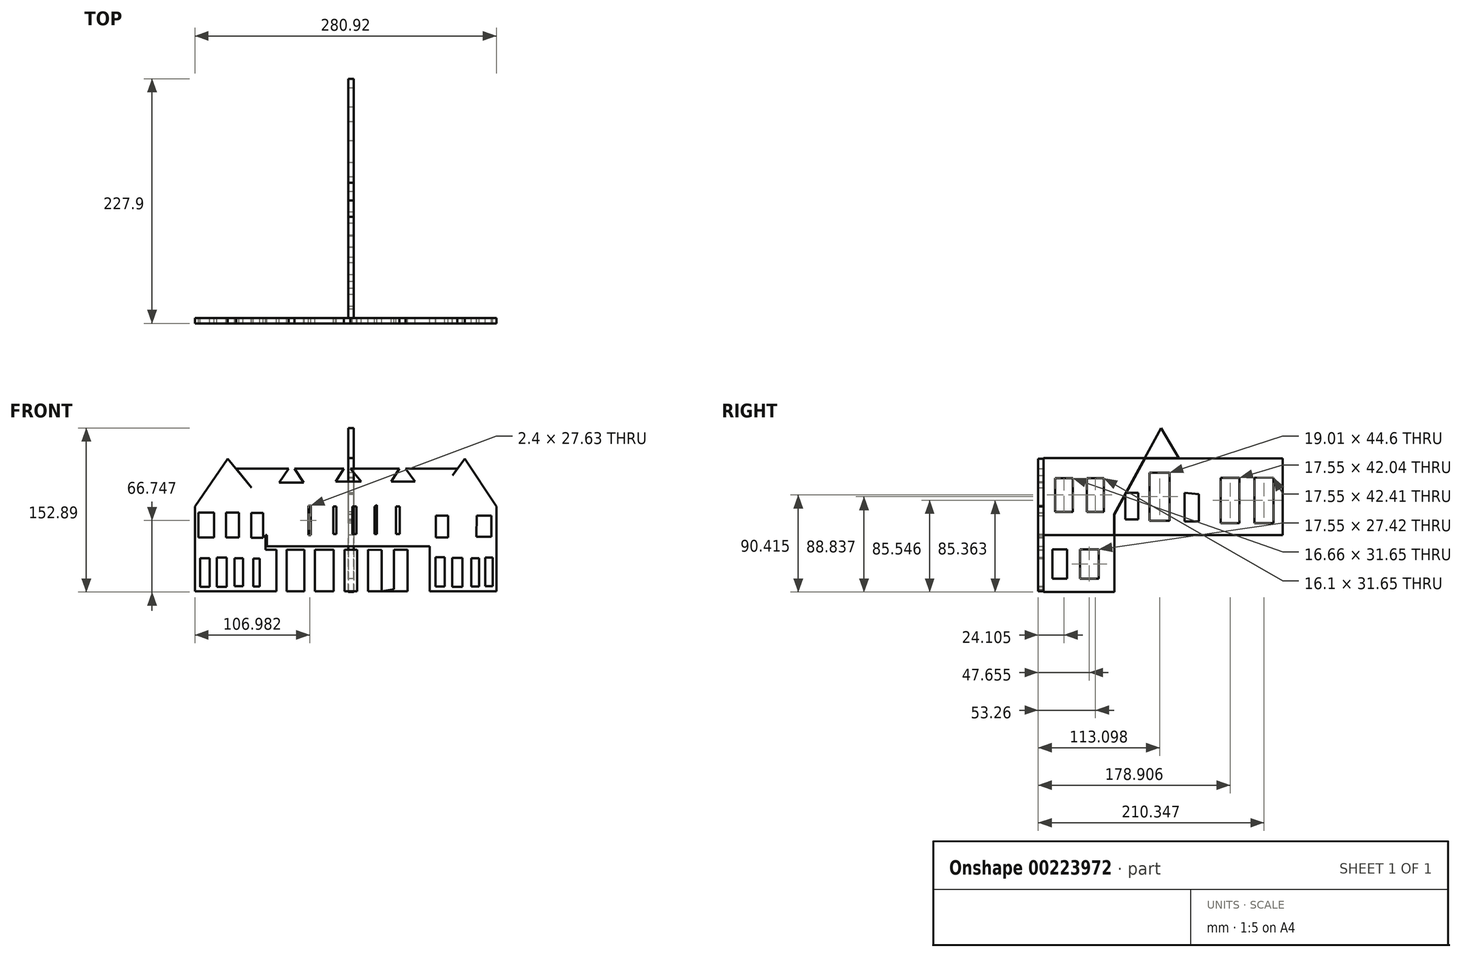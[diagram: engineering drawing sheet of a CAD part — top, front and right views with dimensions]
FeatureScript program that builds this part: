
annotation { "Feature Type Name" : "Feature", "Feature Type Description" : "" }
export const myFeature = defineFeature(function(context is Context, id is Id, definition is map)
    precondition{}
    {
        {
            var Q0;
            Q0=qCreatedBy(makeId("Front.planeOp"),FACE);
            var sketch = newSketch(context, id + "F0", { "sketchPlane" : qUnion([Q0])});
            skLineSegment(sketch, "E0", {"start": v(-37.14, 37.72) * mm, "end": v(-37.14, 10.33) * mm});
            skLineSegment(sketch, "E1", {"start": v(-37.14, 10.33) * mm, "end": v(-34.74, 10.33) * mm});
            skLineSegment(sketch, "E2", {"start": v(-34.74, 10.33) * mm, "end": v(-34.74, 37.96) * mm});
            skLineSegment(sketch, "E3", {"start": v(-34.74, 37.96) * mm, "end": v(-37.14, 37.72) * mm});
            skLineSegment(sketch, "E4", {"start": v(-13.83, 37.24) * mm, "end": v(-13.83, 11.3) * mm});
            skLineSegment(sketch, "E5", {"start": v(-13.83, 11.3) * mm, "end": v(-11.19, 11.3) * mm});
            skLineSegment(sketch, "E6", {"start": v(-11.19, 11.3) * mm, "end": v(-11.19, 37.24) * mm});
            skLineSegment(sketch, "E7", {"start": v(-11.19, 37.24) * mm, "end": v(-13.83, 37.24) * mm});
            skLineSegment(sketch, "E8", {"start": v(3.95, 37.24) * mm, "end": v(3.95, 11.3) * mm});
            skLineSegment(sketch, "E9", {"start": v(3.95, 11.3) * mm, "end": v(7.55, 11.3) * mm});
            skLineSegment(sketch, "E10", {"start": v(7.55, 37.24) * mm, "end": v(3.95, 37.24) * mm});
            skLineSegment(sketch, "E11", {"start": v(7.55, 11.3) * mm, "end": v(7.55, 37.24) * mm});
            skLineSegment(sketch, "E12", {"start": v(24.61, 37.24) * mm, "end": v(24.61, 11.3) * mm});
            skLineSegment(sketch, "E13", {"start": v(24.61, 11.3) * mm, "end": v(26.77, 11.3) * mm});
            skLineSegment(sketch, "E14", {"start": v(26.77, 11.3) * mm, "end": v(26.77, 38.44) * mm});
            skLineSegment(sketch, "E15", {"start": v(26.77, 38.44) * mm, "end": v(24.61, 37.24) * mm});
            skLineSegment(sketch, "E16", {"start": v(44.55, 37.24) * mm, "end": v(44.55, 11.3) * mm});
            skLineSegment(sketch, "E17", {"start": v(44.55, 11.3) * mm, "end": v(47.92, 11.3) * mm});
            skLineSegment(sketch, "E18", {"start": v(47.92, 11.3) * mm, "end": v(47.92, 37.24) * mm});
            skLineSegment(sketch, "E19", {"start": v(47.92, 37.24) * mm, "end": v(44.55, 37.24) * mm});
            skLineSegment(sketch, "E20", {"start": v(77.21, 37.32) * mm, "end": v(107.92, 81.53) * mm});
            skLineSegment(sketch, "E21", {"start": v(107.92, 81.53) * mm, "end": v(138.2, 37.32) * mm});
            skLineSegment(sketch, "E22", {"start": v(138.2, 37.32) * mm, "end": v(77.21, 37.32) * mm});
            skLineSegment(sketch, "E23", {"start": v(138.2, 37.32) * mm, "end": v(138.2, -40.87) * mm});
            skLineSegment(sketch, "E24", {"start": v(138.2, -40.87) * mm, "end": v(77.21, -40.87) * mm});
            skLineSegment(sketch, "E25", {"start": v(-75.9, 37.32) * mm, "end": v(-111.92, 81.53) * mm});
            skLineSegment(sketch, "E26", {"start": v(-111.92, 81.53) * mm, "end": v(-142.62, 37.32) * mm});
            skLineSegment(sketch, "E27", {"start": v(-142.62, 37.32) * mm, "end": v(-75.9, 37.32) * mm});
            skLineSegment(sketch, "E28", {"start": v(-142.62, 29.95) * mm, "end": v(-142.62, 37.32) * mm});
            skLineSegment(sketch, "E29", {"start": v(-142.62, 29.95) * mm, "end": v(-142.62, -40.87) * mm});
            skLineSegment(sketch, "E30", {"start": v(-142.62, -40.87) * mm, "end": v(-75.9, -40.87) * mm});
            skLineSegment(sketch, "E31", {"start": v(-75.9, -40.87) * mm, "end": v(-75.9, 37.32) * mm});
            skLineSegment(sketch, "E32", {"start": v(77.21, -40.87) * mm, "end": v(77.21, 37.32) * mm});
            skLineSegment(sketch, "E33", {"start": v(-104.51, 72.44) * mm, "end": v(101.6, 72.44) * mm});
            skLineSegment(sketch, "E34", {"start": v(-64.56, 59.42) * mm, "end": v(-52.67, 76.55) * mm});
            skPoint(sketch, "E34.startSnap0", {"position": v(-93.9, 59.42) * mm});
            skLineSegment(sketch, "E35", {"start": v(-52.67, 76.55) * mm, "end": v(-41.62, 59.42) * mm});
            skLineSegment(sketch, "E36", {"start": v(-41.62, 59.42) * mm, "end": v(-64.56, 59.42) * mm});
            skLineSegment(sketch, "E37", {"start": v(-11.64, 60.24) * mm, "end": v(-1.45, 76.55) * mm});
            skPoint(sketch, "E37.endSnap0", {"position": v(-1.45, 72.44) * mm});
            skLineSegment(sketch, "E38", {"start": v(-1.45, 76.55) * mm, "end": v(12.22, 60.24) * mm});
            skLineSegment(sketch, "E39", {"start": v(12.22, 60.24) * mm, "end": v(-11.64, 60.24) * mm});
            skLineSegment(sketch, "E40", {"start": v(40.06, 60.24) * mm, "end": v(50.24, 76.55) * mm});
            skLineSegment(sketch, "E41", {"start": v(50.24, 76.55) * mm, "end": v(62.39, 60.24) * mm});
            skLineSegment(sketch, "E42", {"start": v(62.39, 60.24) * mm, "end": v(40.06, 60.24) * mm});
            skLineSegment(sketch, "E43", {"start": v(-142.62, 0) * mm, "end": v(138.2, 0) * mm});
            skLineSegment(sketch, "E44", {"start": v(81.05, 28.12) * mm, "end": v(81.05, 7.63) * mm});
            skLineSegment(sketch, "E45", {"start": v(93.28, 7.63) * mm, "end": v(93.28, 28.12) * mm});
            skLineSegment(sketch, "E46", {"start": v(93.28, 28.12) * mm, "end": v(81.05, 28.12) * mm});
            skLineSegment(sketch, "E47", {"start": v(81.05, 7.63) * mm, "end": v(93.28, 7.63) * mm});
            skLineSegment(sketch, "E48", {"start": v(101.54, 7.63) * mm, "end": v(101.54, 28.43) * mm});
            skLineSegment(sketch, "E49", {"start": v(101.54, 28.43) * mm, "end": v(114.08, 28.43) * mm});
            skLineSegment(sketch, "E50", {"start": v(114.08, 28.43) * mm, "end": v(114.08, 7.63) * mm});
            skLineSegment(sketch, "E51", {"start": v(114.08, 7.63) * mm, "end": v(101.54, 7.63) * mm});
            skLineSegment(sketch, "E52", {"start": v(123.26, 28.43) * mm, "end": v(133.66, 28.43) * mm});
            skLineSegment(sketch, "E53", {"start": v(133.66, 28.43) * mm, "end": v(133.66, 7.63) * mm});
            skLineSegment(sketch, "E54", {"start": v(133.66, 7.63) * mm, "end": v(120.2, 7.63) * mm});
            skLineSegment(sketch, "E55", {"start": v(120.2, 7.63) * mm, "end": v(120.2, 28.43) * mm});
            skLineSegment(sketch, "E56", {"start": v(120.2, 28.43) * mm, "end": v(123.26, 28.43) * mm});
            skLineSegment(sketch, "E57", {"start": v(120.2, 28.43) * mm, "end": v(120.2, 7.63) * mm});
            skLineSegment(sketch, "E58", {"start": v(-138.59, 30.88) * mm, "end": v(-138.59, 8.24) * mm});
            skLineSegment(sketch, "E59", {"start": v(-138.59, 8.24) * mm, "end": v(-125.74, 8.24) * mm});
            skLineSegment(sketch, "E60", {"start": v(-125.74, 8.24) * mm, "end": v(-125.74, 30.88) * mm});
            skLineSegment(sketch, "E61", {"start": v(-125.74, 30.88) * mm, "end": v(-138.59, 30.88) * mm});
            skLineSegment(sketch, "E62", {"start": v(-114.11, 8.24) * mm, "end": v(-114.11, 30.88) * mm});
            skLineSegment(sketch, "E63", {"start": v(-114.11, 30.88) * mm, "end": v(-102.18, 30.88) * mm});
            skLineSegment(sketch, "E64", {"start": v(-102.18, 30.88) * mm, "end": v(-102.18, 8.24) * mm});
            skLineSegment(sketch, "E65", {"start": v(-102.18, 8.24) * mm, "end": v(-114.11, 8.24) * mm});
            skLineSegment(sketch, "E66", {"start": v(-90.25, 8.24) * mm, "end": v(-90.25, 30.88) * mm});
            skLineSegment(sketch, "E67", {"start": v(-90.25, 30.88) * mm, "end": v(-79.85, 30.88) * mm});
            skLineSegment(sketch, "E68", {"start": v(-79.85, 30.88) * mm, "end": v(-79.85, 8.24) * mm});
            skLineSegment(sketch, "E69", {"start": v(-79.85, 8.24) * mm, "end": v(-90.25, 8.24) * mm});
            skLineSegment(sketch, "E70", {"start": v(-138.28, -20.2) * mm, "end": v(-138.28, -37.03) * mm});
            skLineSegment(sketch, "E71", {"start": v(-138.28, -37.03) * mm, "end": v(-129.71, -37.03) * mm});
            skLineSegment(sketch, "E72", {"start": v(-129.71, -37.03) * mm, "end": v(-129.71, -18.07) * mm});
            skLineSegment(sketch, "E73", {"start": v(-138.28, -20.2) * mm, "end": v(-138.28, -11.34) * mm});
            skLineSegment(sketch, "E74", {"start": v(-138.28, -11.34) * mm, "end": v(-129.71, -11.34) * mm});
            skLineSegment(sketch, "E75", {"start": v(-129.71, -11.34) * mm, "end": v(-129.71, -18.07) * mm});
            skLineSegment(sketch, "E76", {"start": v(-122.07, -37.03) * mm, "end": v(-122.07, -11.03) * mm});
            skLineSegment(sketch, "E77", {"start": v(-122.07, -11.03) * mm, "end": v(-113.5, -11.03) * mm});
            skLineSegment(sketch, "E78", {"start": v(-113.5, -11.03) * mm, "end": v(-113.5, -37.03) * mm});
            skLineSegment(sketch, "E79", {"start": v(-113.5, -37.03) * mm, "end": v(-122.07, -37.03) * mm});
            skLineSegment(sketch, "E80", {"start": v(-105.85, -37.03) * mm, "end": v(-105.85, -11.03) * mm});
            skLineSegment(sketch, "E81", {"start": v(-105.85, -11.03) * mm, "end": v(-97.29, -11.03) * mm});
            skLineSegment(sketch, "E82", {"start": v(-97.29, -11.03) * mm, "end": v(-97.29, -37.03) * mm});
            skLineSegment(sketch, "E83", {"start": v(-97.29, -37.03) * mm, "end": v(-105.85, -37.03) * mm});
            skLineSegment(sketch, "E84", {"start": v(-89.64, -37.03) * mm, "end": v(-89.64, -11.03) * mm});
            skLineSegment(sketch, "E85", {"start": v(-89.64, -11.03) * mm, "end": v(-81.08, -11.03) * mm});
            skLineSegment(sketch, "E86", {"start": v(-81.08, -11.03) * mm, "end": v(-81.08, -37.03) * mm});
            skLineSegment(sketch, "E87", {"start": v(-81.08, -37.03) * mm, "end": v(-89.64, -37.03) * mm});
            skLineSegment(sketch, "E88", {"start": v(81.96, -33.97) * mm, "end": v(81.96, -11.03) * mm});
            skLineSegment(sketch, "E89", {"start": v(81.96, -11.03) * mm, "end": v(89.92, -11.03) * mm});
            skLineSegment(sketch, "E90", {"start": v(89.92, -11.03) * mm, "end": v(89.92, -37.03) * mm});
            skLineSegment(sketch, "E91", {"start": v(81.96, -33.97) * mm, "end": v(81.96, -37.03) * mm});
            skLineSegment(sketch, "E92", {"start": v(81.96, -37.03) * mm, "end": v(89.92, -37.03) * mm});
            skLineSegment(sketch, "E93", {"start": v(96.65, -37.03) * mm, "end": v(96.65, -11.03) * mm});
            skLineSegment(sketch, "E94", {"start": v(96.65, -11.03) * mm, "end": v(106.44, -11.03) * mm});
            skLineSegment(sketch, "E95", {"start": v(106.44, -11.03) * mm, "end": v(106.44, -37.03) * mm});
            skLineSegment(sketch, "E96", {"start": v(96.65, -37.03) * mm, "end": v(106.44, -37.03) * mm});
            skLineSegment(sketch, "E97", {"start": v(114.08, -37.03) * mm, "end": v(114.08, -11.03) * mm});
            skLineSegment(sketch, "E98", {"start": v(114.08, -11.03) * mm, "end": v(121.73, -11.03) * mm});
            skLineSegment(sketch, "E99", {"start": v(121.73, -11.03) * mm, "end": v(121.73, -37.03) * mm});
            skLineSegment(sketch, "E100", {"start": v(121.73, -37.03) * mm, "end": v(114.08, -37.03) * mm});
            skLineSegment(sketch, "E101", {"start": v(127.54, -11.03) * mm, "end": v(127.54, -37.03) * mm});
            skLineSegment(sketch, "E102", {"start": v(127.54, -37.03) * mm, "end": v(134.27, -37.03) * mm});
            skLineSegment(sketch, "E103", {"start": v(134.27, -37.03) * mm, "end": v(134.27, -11.03) * mm});
            skLineSegment(sketch, "E104", {"start": v(134.27, -11.03) * mm, "end": v(127.54, -11.03) * mm});
            skSolve(sketch);
        }
        {
            var Q0;
            Q0=qCreatedBy(makeId("Right.planeOp"),FACE);
            var sketch = newSketch(context, id + "F1", { "sketchPlane" : qUnion([Q0])});
            skLineSegment(sketch, "E105", {"start": v(0, 82.22) * mm, "end": v(55.54, 82.22) * mm});
            skLineSegment(sketch, "E106", {"start": v(0, 82.22) * mm, "end": v(0, -42.77) * mm});
            skLineSegment(sketch, "E107", {"start": v(0, -42.77) * mm, "end": v(141.8, -42.77) * mm});
            skLineSegment(sketch, "E108", {"start": v(141.8, 82.22) * mm, "end": v(55.54, 82.22) * mm});
            skLineSegment(sketch, "E109", {"start": v(141.8, 82.22) * mm, "end": v(222.59, 82.22) * mm});
            skLineSegment(sketch, "E110", {"start": v(222.59, 82.22) * mm, "end": v(222.59, -42.77) * mm});
            skLineSegment(sketch, "E111", {"start": v(222.59, -42.77) * mm, "end": v(141.8, -42.77) * mm});
            skLineSegment(sketch, "E112", {"start": v(65.67, 29.77) * mm, "end": v(109.54, 110.29) * mm});
            skLineSegment(sketch, "E113", {"start": v(109.54, 110.29) * mm, "end": v(156.19, 29.77) * mm});
            skLineSegment(sketch, "E114", {"start": v(65.67, 29.77) * mm, "end": v(65.67, -42.77) * mm});
            skLineSegment(sketch, "E115", {"start": v(65.67, -42.77) * mm, "end": v(156.19, -42.77) * mm});
            skLineSegment(sketch, "E116", {"start": v(156.19, -42.77) * mm, "end": v(156.19, 29.77) * mm});
            skLineSegment(sketch, "E117", {"start": v(0, 10.33) * mm, "end": v(222.59, 10.33) * mm});
            skLineSegment(sketch, "E118.bottom", {"start": v(10.7, 63.64) * mm, "end": v(27.36, 63.64) * mm});
            skLineSegment(sketch, "E118.top", {"start": v(10.7, 31.99) * mm, "end": v(27.36, 31.99) * mm});
            skLineSegment(sketch, "E118.left", {"start": v(10.7, 63.64) * mm, "end": v(10.7, 31.99) * mm});
            skLineSegment(sketch, "E118.right", {"start": v(27.36, 63.64) * mm, "end": v(27.36, 31.99) * mm});
            skPoint(sketch, "E119.firstSnap0", {"position": v(19.03, 63.64) * mm});
            skLineSegment(sketch, "E119.bottom", {"start": v(40.13, 63.64) * mm, "end": v(56.23, 63.64) * mm});
            skLineSegment(sketch, "E119.top", {"start": v(40.13, 31.99) * mm, "end": v(56.23, 31.99) * mm});
            skLineSegment(sketch, "E119.left", {"start": v(40.13, 63.64) * mm, "end": v(40.13, 31.99) * mm});
            skLineSegment(sketch, "E119.right", {"start": v(56.23, 63.64) * mm, "end": v(56.23, 31.99) * mm});
            skLineSegment(sketch, "E120.bottom", {"start": v(76.55, 49.73) * mm, "end": v(89, 49.73) * mm});
            skLineSegment(sketch, "E120.top", {"start": v(76.55, 24.77) * mm, "end": v(89, 24.77) * mm});
            skLineSegment(sketch, "E120.left", {"start": v(76.55, 49.73) * mm, "end": v(76.55, 24.77) * mm});
            skLineSegment(sketch, "E120.right", {"start": v(89, 49.73) * mm, "end": v(89, 24.77) * mm});
            skLineSegment(sketch, "E121.bottom", {"start": v(99, 68.64) * mm, "end": v(117.32, 68.64) * mm});
            skLineSegment(sketch, "E121.top", {"start": v(99, 24.77) * mm, "end": v(117.32, 24.77) * mm});
            skLineSegment(sketch, "E121.left", {"start": v(99, 68.64) * mm, "end": v(99, 24.77) * mm});
            skLineSegment(sketch, "E121.right", {"start": v(117.32, 68.64) * mm, "end": v(117.32, 24.77) * mm});
            skPoint(sketch, "E122.firstSnap0", {"position": v(82.77, 49.73) * mm});
            skPoint(sketch, "E122.oppositeSnap0", {"position": v(108.15, 24.77) * mm});
            skLineSegment(sketch, "E122.bottom", {"start": v(144.62, 49.73) * mm, "end": v(131.2, 49.73) * mm});
            skLineSegment(sketch, "E122.top", {"start": v(144.62, 24.77) * mm, "end": v(131.2, 24.77) * mm});
            skLineSegment(sketch, "E122.left", {"start": v(144.62, 49.73) * mm, "end": v(144.62, 24.77) * mm});
            skLineSegment(sketch, "E122.right", {"start": v(131.2, 49.73) * mm, "end": v(131.2, 24.77) * mm});
            skLineSegment(sketch, "E123.bottom", {"start": v(213.39, 63.64) * mm, "end": v(195.62, 63.64) * mm});
            skLineSegment(sketch, "E123.top", {"start": v(213.39, 22.55) * mm, "end": v(195.62, 22.55) * mm});
            skLineSegment(sketch, "E123.left", {"start": v(213.39, 63.64) * mm, "end": v(213.39, 22.55) * mm});
            skLineSegment(sketch, "E123.right", {"start": v(195.62, 63.64) * mm, "end": v(195.62, 22.55) * mm});
            skPoint(sketch, "E124.oppositeSnap0", {"position": v(182.2, 82.22) * mm});
            skLineSegment(sketch, "E124.bottom", {"start": v(166.74, 63.64) * mm, "end": v(182.2, 63.64) * mm});
            skLineSegment(sketch, "E124.top", {"start": v(166.74, 22.55) * mm, "end": v(182.2, 22.55) * mm});
            skLineSegment(sketch, "E124.left", {"start": v(166.74, 63.64) * mm, "end": v(166.74, 22.55) * mm});
            skLineSegment(sketch, "E124.right", {"start": v(182.2, 63.64) * mm, "end": v(182.2, 22.55) * mm});
            skLineSegment(sketch, "E125.bottom", {"start": v(7.92, 0) * mm, "end": v(21.8, 0) * mm});
            skLineSegment(sketch, "E125.top", {"start": v(7.92, -29.1) * mm, "end": v(21.8, -29.1) * mm});
            skLineSegment(sketch, "E125.left", {"start": v(7.92, 0) * mm, "end": v(7.92, -29.1) * mm});
            skLineSegment(sketch, "E125.right", {"start": v(21.8, 0) * mm, "end": v(21.8, -29.1) * mm});
            skLineSegment(sketch, "E126.bottom", {"start": v(35.68, -3) * mm, "end": v(51.23, -3) * mm});
            skLineSegment(sketch, "E126.top", {"start": v(35.68, -28.54) * mm, "end": v(51.23, -28.54) * mm});
            skLineSegment(sketch, "E126.left", {"start": v(35.68, -3) * mm, "end": v(35.68, -28.54) * mm});
            skLineSegment(sketch, "E126.right", {"start": v(51.23, -3) * mm, "end": v(51.23, -28.54) * mm});
            skLineSegment(sketch, "E127.bottom", {"start": v(77.33, 0) * mm, "end": v(92.33, 0) * mm});
            skLineSegment(sketch, "E127.top", {"start": v(77.33, -29.65) * mm, "end": v(92.33, -29.65) * mm});
            skLineSegment(sketch, "E127.left", {"start": v(77.33, 0) * mm, "end": v(77.33, -29.65) * mm});
            skLineSegment(sketch, "E127.right", {"start": v(92.33, 0) * mm, "end": v(92.33, -29.65) * mm});
            skLineSegment(sketch, "E128.bottom", {"start": v(106.77, 0) * mm, "end": v(123.43, 0) * mm});
            skLineSegment(sketch, "E128.top", {"start": v(106.77, -29.65) * mm, "end": v(123.43, -29.65) * mm});
            skLineSegment(sketch, "E128.left", {"start": v(106.77, 0) * mm, "end": v(106.77, -29.65) * mm});
            skLineSegment(sketch, "E128.right", {"start": v(123.43, 0) * mm, "end": v(123.43, -29.65) * mm});
            skLineSegment(sketch, "E129.bottom", {"start": v(134.53, 0) * mm, "end": v(149.53, 0) * mm});
            skLineSegment(sketch, "E129.top", {"start": v(134.53, -29.65) * mm, "end": v(149.53, -29.65) * mm});
            skLineSegment(sketch, "E129.left", {"start": v(134.53, 0) * mm, "end": v(134.53, -29.65) * mm});
            skLineSegment(sketch, "E129.right", {"start": v(149.53, 0) * mm, "end": v(149.53, -29.65) * mm});
            skLineSegment(sketch, "E130.bottom", {"start": v(166.74, 0) * mm, "end": v(184.51, 0) * mm});
            skLineSegment(sketch, "E130.top", {"start": v(166.74, -29.65) * mm, "end": v(184.51, -29.65) * mm});
            skLineSegment(sketch, "E130.left", {"start": v(166.74, 0) * mm, "end": v(166.74, -29.65) * mm});
            skLineSegment(sketch, "E130.right", {"start": v(184.51, 0) * mm, "end": v(184.51, -29.65) * mm});
            skLineSegment(sketch, "E131.bottom", {"start": v(198.4, 0) * mm, "end": v(215.05, 0) * mm});
            skLineSegment(sketch, "E131.top", {"start": v(198.4, -29.65) * mm, "end": v(215.05, -29.65) * mm});
            skLineSegment(sketch, "E131.left", {"start": v(198.4, 0) * mm, "end": v(198.4, -29.65) * mm});
            skLineSegment(sketch, "E131.right", {"start": v(215.05, 0) * mm, "end": v(215.05, -29.65) * mm});
            skSolve(sketch);
        }
        {
            var Q0;
            Q0=qCreatedBy(makeId("Right.planeOp"),FACE);
            var sketch = newSketch(context, id + "F2", { "sketchPlane" : qUnion([Q0])});
            skLineSegment(sketch, "E132", {"start": v(3.1, 82.07) * mm, "end": v(222.82, 82.07) * mm});
            skLineSegment(sketch, "E133", {"start": v(222.82, 82.07) * mm, "end": v(222.82, -42.6) * mm});
            skLineSegment(sketch, "E134", {"start": v(222.82, -42.6) * mm, "end": v(0, -42.6) * mm});
            skLineSegment(sketch, "E135", {"start": v(0, -42.6) * mm, "end": v(0, 79.14) * mm});
            skLineSegment(sketch, "E136", {"start": v(27.22, 64.15) * mm, "end": v(11.13, 64.15) * mm});
            skLineSegment(sketch, "E137", {"start": v(11.13, 64.15) * mm, "end": v(11.13, 31.61) * mm});
            skLineSegment(sketch, "E138", {"start": v(11.13, 31.61) * mm, "end": v(27.59, 31.61) * mm});
            skLineSegment(sketch, "E139", {"start": v(27.59, 31.61) * mm, "end": v(27.22, 64.15) * mm});
            skLineSegment(sketch, "E140", {"start": v(56.83, 64.15) * mm, "end": v(56.83, 32.34) * mm});
            skLineSegment(sketch, "E141", {"start": v(56.83, 32.34) * mm, "end": v(40.38, 32.34) * mm});
            skLineSegment(sketch, "E142", {"start": v(40.38, 32.34) * mm, "end": v(40.38, 64.15) * mm});
            skLineSegment(sketch, "E143", {"start": v(40.38, 64.15) * mm, "end": v(56.83, 64.15) * mm});
            skLineSegment(sketch, "E144", {"start": v(109.48, 109.85) * mm, "end": v(156.28, 28.32) * mm});
            skLineSegment(sketch, "E145", {"start": v(156.28, 28.32) * mm, "end": v(156.28, -42.6) * mm});
            skLineSegment(sketch, "E146", {"start": v(109.48, 109.85) * mm, "end": v(65.97, 29.42) * mm});
            skLineSegment(sketch, "E147", {"start": v(65.97, 29.42) * mm, "end": v(65.97, -42.6) * mm});
            skLineSegment(sketch, "E148", {"start": v(222.82, 10.4) * mm, "end": v(0, 10.4) * mm});
            skLineSegment(sketch, "E149", {"start": v(3.1, 0) * mm, "end": v(222.82, 0) * mm});
            skLineSegment(sketch, "E150", {"start": v(222.82, 0) * mm, "end": v(215.87, 0) * mm});
            skLineSegment(sketch, "E151", {"start": v(215.87, 0) * mm, "end": v(215.87, -28.35) * mm});
            skLineSegment(sketch, "E152", {"start": v(215.87, -28.35) * mm, "end": v(198.32, -28.35) * mm});
            skLineSegment(sketch, "E153", {"start": v(198.32, -28.35) * mm, "end": v(198.32, 0) * mm});
            skLineSegment(sketch, "E154", {"start": v(198.32, 0) * mm, "end": v(186.26, 0) * mm});
            skLineSegment(sketch, "E155", {"start": v(186.26, 0) * mm, "end": v(186.26, -29.44) * mm});
            skLineSegment(sketch, "E156", {"start": v(186.26, -29.44) * mm, "end": v(166.15, -29.44) * mm});
            skLineSegment(sketch, "E157", {"start": v(166.15, -29.44) * mm, "end": v(166.15, 0) * mm});
            skLineSegment(sketch, "E158", {"start": v(166.15, 0) * mm, "end": v(149.33, 0) * mm});
            skLineSegment(sketch, "E159", {"start": v(149.33, 0) * mm, "end": v(149.33, -29.8) * mm});
            skLineSegment(sketch, "E160", {"start": v(149.33, -29.8) * mm, "end": v(134.34, -29.8) * mm});
            skLineSegment(sketch, "E161", {"start": v(134.34, -29.8) * mm, "end": v(134.34, 0) * mm});
            skLineSegment(sketch, "E162", {"start": v(134.34, 0) * mm, "end": v(149.33, 0) * mm});
            skLineSegment(sketch, "E163", {"start": v(124.1, 0) * mm, "end": v(124.1, -30.17) * mm});
            skLineSegment(sketch, "E164", {"start": v(124.1, -30.17) * mm, "end": v(106.19, -30.17) * mm});
            skLineSegment(sketch, "E165", {"start": v(106.19, -30.17) * mm, "end": v(106.19, 0) * mm});
            skLineSegment(sketch, "E166", {"start": v(106.19, 0) * mm, "end": v(124.1, 0) * mm});
            skLineSegment(sketch, "E167", {"start": v(91.57, 0) * mm, "end": v(91.57, -30.17) * mm});
            skLineSegment(sketch, "E168", {"start": v(91.57, -30.17) * mm, "end": v(77.3, -30.17) * mm});
            skLineSegment(sketch, "E169", {"start": v(77.3, -30.17) * mm, "end": v(77.3, 0) * mm});
            skLineSegment(sketch, "E170", {"start": v(77.3, 0) * mm, "end": v(91.57, 0) * mm});
            skLineSegment(sketch, "E171", {"start": v(51.35, -2.75) * mm, "end": v(51.35, -30.17) * mm});
            skPoint(sketch, "E171.endSnap0", {"position": v(84.44, -30.17) * mm});
            skLineSegment(sketch, "E172", {"start": v(51.35, -30.17) * mm, "end": v(33.8, -30.17) * mm});
            skLineSegment(sketch, "E173", {"start": v(33.8, -30.17) * mm, "end": v(33.8, -2.75) * mm});
            skLineSegment(sketch, "E174", {"start": v(33.8, -2.75) * mm, "end": v(51.35, -2.75) * mm});
            skLineSegment(sketch, "E175", {"start": v(21.74, -2.75) * mm, "end": v(21.74, -30.17) * mm});
            skLineSegment(sketch, "E176", {"start": v(21.74, -30.17) * mm, "end": v(8.2, -30.17) * mm});
            skLineSegment(sketch, "E177", {"start": v(8.2, -30.17) * mm, "end": v(8.2, -2.75) * mm});
            skLineSegment(sketch, "E178", {"start": v(8.2, -2.75) * mm, "end": v(21.74, -2.75) * mm});
            skLineSegment(sketch, "E179", {"start": v(214.04, 63.79) * mm, "end": v(214.04, 21.74) * mm});
            skLineSegment(sketch, "E180", {"start": v(214.04, 21.74) * mm, "end": v(196.5, 21.74) * mm});
            skLineSegment(sketch, "E181", {"start": v(196.5, 21.74) * mm, "end": v(196.5, 64.15) * mm});
            skLineSegment(sketch, "E182", {"start": v(196.5, 64.15) * mm, "end": v(214.04, 63.79) * mm});
            skLineSegment(sketch, "E183", {"start": v(182.6, 63.79) * mm, "end": v(182.6, 21.74) * mm});
            skLineSegment(sketch, "E184", {"start": v(182.6, 21.74) * mm, "end": v(165.05, 21.74) * mm});
            skLineSegment(sketch, "E185", {"start": v(165.05, 21.74) * mm, "end": v(165.05, 63.79) * mm});
            skLineSegment(sketch, "E186", {"start": v(165.05, 63.79) * mm, "end": v(182.6, 63.79) * mm});
            skLineSegment(sketch, "E187", {"start": v(117.52, 69.63) * mm, "end": v(117.52, 23.93) * mm});
            skPoint(sketch, "E187.startSnap0", {"position": v(87.73, 69.63) * mm});
            skLineSegment(sketch, "E188", {"start": v(117.52, 23.93) * mm, "end": v(98.51, 23.93) * mm});
            skLineSegment(sketch, "E189", {"start": v(98.51, 23.93) * mm, "end": v(98.51, 68.54) * mm});
            skLineSegment(sketch, "E190", {"start": v(98.51, 68.54) * mm, "end": v(121.18, 68.54) * mm});
            skLineSegment(sketch, "E191", {"start": v(131.42, 49.9) * mm, "end": v(131.42, 23.2) * mm});
            skLineSegment(sketch, "E192", {"start": v(131.42, 23.2) * mm, "end": v(144.58, 23.2) * mm});
            skLineSegment(sketch, "E193", {"start": v(144.58, 23.2) * mm, "end": v(144.58, 48.7) * mm});
            skLineSegment(sketch, "E194", {"start": v(144.58, 48.7) * mm, "end": v(131.42, 49.9) * mm});
            skLineSegment(sketch, "E195", {"start": v(88.28, 49.9) * mm, "end": v(88.28, 25.03) * mm});
            skLineSegment(sketch, "E196", {"start": v(88.28, 25.03) * mm, "end": v(76.21, 25.03) * mm});
            skLineSegment(sketch, "E197", {"start": v(76.21, 25.03) * mm, "end": v(76.21, 49.9) * mm});
            skLineSegment(sketch, "E198", {"start": v(76.21, 49.9) * mm, "end": v(88.28, 49.9) * mm});
            skSolve(sketch);
        }
        {
            var Q0;
            Q0=qCreatedBy(makeId("Front.planeOp"),FACE);
            var sketch = newSketch(context, id + "F3", { "sketchPlane" : qUnion([Q0])});
            skLineSegment(sketch, "E199", {"start": v(108.7, 81.73) * mm, "end": v(138, 37.2) * mm});
            skLineSegment(sketch, "E200", {"start": v(138, 37.2) * mm, "end": v(138, -41.98) * mm});
            skLineSegment(sketch, "E201", {"start": v(138, -41.98) * mm, "end": v(-142.92, -41.98) * mm});
            skLineSegment(sketch, "E202", {"start": v(-142.92, -41.98) * mm, "end": v(-142.92, 37.2) * mm});
            skLineSegment(sketch, "E203", {"start": v(-142.92, 37.2) * mm, "end": v(-112.46, 81.73) * mm});
            skLineSegment(sketch, "E204", {"start": v(-112.46, 81.73) * mm, "end": v(-75.54, 37.2) * mm});
            skLineSegment(sketch, "E205", {"start": v(-75.54, 37.2) * mm, "end": v(75.96, 37.2) * mm});
            skLineSegment(sketch, "E206", {"start": v(75.96, 37.2) * mm, "end": v(108.7, 81.73) * mm});
            skLineSegment(sketch, "E207", {"start": v(101.98, 72.6) * mm, "end": v(68.73, 72.6) * mm});
            skLineSegment(sketch, "E208", {"start": v(68.73, 72.6) * mm, "end": v(53.5, 72.6) * mm});
            skLineSegment(sketch, "E209", {"start": v(53.5, 72.6) * mm, "end": v(-104.9, 72.6) * mm});
            skLineSegment(sketch, "E210", {"start": v(-51.94, 77.16) * mm, "end": v(-41.66, 58.5) * mm});
            skLineSegment(sketch, "E211", {"start": v(-41.66, 58.5) * mm, "end": v(-65.26, 58.5) * mm});
            skLineSegment(sketch, "E212", {"start": v(-65.26, 58.5) * mm, "end": v(-51.94, 77.16) * mm});
            skLineSegment(sketch, "E213", {"start": v(0, 77.16) * mm, "end": v(13.34, 61.07) * mm});
            skLineSegment(sketch, "E214", {"start": v(13.34, 61.07) * mm, "end": v(-12.35, 61.07) * mm});
            skLineSegment(sketch, "E215", {"start": v(-12.35, 61.07) * mm, "end": v(0, 77.16) * mm});
            skLineSegment(sketch, "E216", {"start": v(50.45, 77.16) * mm, "end": v(63.8, 61.06) * mm});
            skLineSegment(sketch, "E217", {"start": v(63.8, 61.06) * mm, "end": v(40.18, 61.06) * mm});
            skLineSegment(sketch, "E218", {"start": v(40.18, 61.06) * mm, "end": v(49.7, 76.78) * mm});
            skLineSegment(sketch, "E219", {"start": v(138, 37.2) * mm, "end": v(75.96, 37.2) * mm});
            skLineSegment(sketch, "E220", {"start": v(81.67, 28.44) * mm, "end": v(81.67, 8.26) * mm});
            skLineSegment(sketch, "E221", {"start": v(81.67, 8.26) * mm, "end": v(93.09, 8.26) * mm});
            skLineSegment(sketch, "E222", {"start": v(93.09, 8.26) * mm, "end": v(93.09, 28.44) * mm});
            skLineSegment(sketch, "E223", {"start": v(93.09, 28.44) * mm, "end": v(81.67, 28.44) * mm});
            skLineSegment(sketch, "E224", {"start": v(101.84, 28.44) * mm, "end": v(114.78, 28.44) * mm});
            skLineSegment(sketch, "E225", {"start": v(114.78, 28.44) * mm, "end": v(114.78, 7.12) * mm});
            skLineSegment(sketch, "E226", {"start": v(114.78, 7.12) * mm, "end": v(101.08, 7.12) * mm});
            skLineSegment(sketch, "E227", {"start": v(101.08, 7.12) * mm, "end": v(101.46, 27.3) * mm});
            skLineSegment(sketch, "E228", {"start": v(119.73, 28.44) * mm, "end": v(133.44, 28.44) * mm});
            skLineSegment(sketch, "E229", {"start": v(133.44, 28.44) * mm, "end": v(133.44, 9.02) * mm});
            skLineSegment(sketch, "E230", {"start": v(133.44, 9.02) * mm, "end": v(119.35, 9.02) * mm});
            skLineSegment(sketch, "E231", {"start": v(119.35, 9.02) * mm, "end": v(119.73, 28.44) * mm});
            skLineSegment(sketch, "E232", {"start": v(75.96, 37.2) * mm, "end": v(75.96, -41.98) * mm});
            skLineSegment(sketch, "E233", {"start": v(75.96, -41.98) * mm, "end": v(75.96, 10.55) * mm});
            skLineSegment(sketch, "E234", {"start": v(75.96, 10.55) * mm, "end": v(-77.06, 10.55) * mm});
            skLineSegment(sketch, "E235", {"start": v(-77.06, 10.55) * mm, "end": v(-77.06, -3.16) * mm});
            skLineSegment(sketch, "E236", {"start": v(-77.06, -3.16) * mm, "end": v(75.96, -3.16) * mm});
            skLineSegment(sketch, "E237", {"start": v(75.96, -3.16) * mm, "end": v(66.82, -3.16) * mm});
            skLineSegment(sketch, "E238", {"start": v(66.82, -3.16) * mm, "end": v(66.82, -41.98) * mm});
            skLineSegment(sketch, "E239", {"start": v(66.82, -41.98) * mm, "end": v(55.4, -41.98) * mm});
            skLineSegment(sketch, "E240", {"start": v(55.4, -41.98) * mm, "end": v(55.4, -3.16) * mm});
            skLineSegment(sketch, "E241", {"start": v(55.4, -3.16) * mm, "end": v(42.46, -3.16) * mm});
            skLineSegment(sketch, "E242", {"start": v(42.46, -3.16) * mm, "end": v(42.46, -40.08) * mm});
            skLineSegment(sketch, "E243", {"start": v(42.46, -40.08) * mm, "end": v(31.04, -41.98) * mm});
            skLineSegment(sketch, "E244", {"start": v(31.04, -41.98) * mm, "end": v(31.04, -3.54) * mm});
            skLineSegment(sketch, "E245", {"start": v(31.04, -3.54) * mm, "end": v(18.48, -3.16) * mm});
            skLineSegment(sketch, "E246", {"start": v(18.48, -3.16) * mm, "end": v(18.48, -41.98) * mm});
            skLineSegment(sketch, "E247", {"start": v(18.48, -41.98) * mm, "end": v(8.2, -41.98) * mm});
            skLineSegment(sketch, "E248", {"start": v(8.2, -41.98) * mm, "end": v(8.2, -3.16) * mm});
            skLineSegment(sketch, "E249", {"start": v(8.2, -3.16) * mm, "end": v(-3.6, -3.16) * mm});
            skLineSegment(sketch, "E250", {"start": v(-3.6, -3.16) * mm, "end": v(-3.6, -41.98) * mm});
            skLineSegment(sketch, "E251", {"start": v(-13.5, -3.16) * mm, "end": v(-13.5, -41.98) * mm});
            skLineSegment(sketch, "E252", {"start": v(-31, -3.16) * mm, "end": v(-31, -41.98) * mm});
            skLineSegment(sketch, "E253", {"start": v(-40.9, -3.16) * mm, "end": v(-40.9, -41.98) * mm});
            skLineSegment(sketch, "E254", {"start": v(-57.27, -3.16) * mm, "end": v(-57.27, -41.98) * mm});
            skLineSegment(sketch, "E255", {"start": v(-66.79, -3.16) * mm, "end": v(-66.79, -41.98) * mm});
            skLineSegment(sketch, "E256", {"start": v(-77.06, -3.16) * mm, "end": v(-77.06, -41.98) * mm});
            skLineSegment(sketch, "E257", {"start": v(-77.06, -41.98) * mm, "end": v(-75.16, -41.22) * mm});
            skLineSegment(sketch, "E258.bottom", {"start": v(134.58, -10.39) * mm, "end": v(127.73, -10.39) * mm});
            skLineSegment(sketch, "E258.top", {"start": v(134.58, -37.03) * mm, "end": v(127.73, -37.03) * mm});
            skLineSegment(sketch, "E258.left", {"start": v(134.58, -10.39) * mm, "end": v(134.58, -37.03) * mm});
            skLineSegment(sketch, "E258.right", {"start": v(127.73, -10.39) * mm, "end": v(127.73, -37.03) * mm});
            skLineSegment(sketch, "E259.bottom", {"start": v(122.02, -11.15) * mm, "end": v(114.78, -11.15) * mm});
            skLineSegment(sketch, "E259.top", {"start": v(122.02, -37.41) * mm, "end": v(114.78, -37.41) * mm});
            skLineSegment(sketch, "E259.left", {"start": v(122.02, -11.15) * mm, "end": v(122.02, -37.41) * mm});
            skLineSegment(sketch, "E259.right", {"start": v(114.78, -11.15) * mm, "end": v(114.78, -37.41) * mm});
            skLineSegment(sketch, "E260.bottom", {"start": v(106.41, -10.77) * mm, "end": v(96.9, -10.77) * mm});
            skLineSegment(sketch, "E260.top", {"start": v(106.41, -37.8) * mm, "end": v(96.9, -37.8) * mm});
            skLineSegment(sketch, "E260.left", {"start": v(106.41, -10.77) * mm, "end": v(106.41, -37.8) * mm});
            skLineSegment(sketch, "E260.right", {"start": v(96.9, -10.77) * mm, "end": v(96.9, -37.8) * mm});
            skLineSegment(sketch, "E261.bottom", {"start": v(90.04, -10) * mm, "end": v(81.29, -10) * mm});
            skLineSegment(sketch, "E261.top", {"start": v(90.04, -37.41) * mm, "end": v(81.29, -37.41) * mm});
            skLineSegment(sketch, "E261.left", {"start": v(90.04, -10) * mm, "end": v(90.04, -37.41) * mm});
            skLineSegment(sketch, "E261.right", {"start": v(81.29, -10) * mm, "end": v(81.29, -37.41) * mm});
            skLineSegment(sketch, "E262.bottom", {"start": v(-79.35, 31.1) * mm, "end": v(-90.39, 31.1) * mm});
            skLineSegment(sketch, "E262.top", {"start": v(-79.35, 7.88) * mm, "end": v(-90.39, 7.88) * mm});
            skLineSegment(sketch, "E262.left", {"start": v(-79.35, 31.1) * mm, "end": v(-79.35, 7.88) * mm});
            skLineSegment(sketch, "E262.right", {"start": v(-90.39, 31.1) * mm, "end": v(-90.39, 7.88) * mm});
            skLineSegment(sketch, "E263.bottom", {"start": v(-101.8, 31.48) * mm, "end": v(-113.99, 31.48) * mm});
            skLineSegment(sketch, "E263.top", {"start": v(-101.8, 8.26) * mm, "end": v(-113.99, 8.26) * mm});
            skLineSegment(sketch, "E263.left", {"start": v(-101.8, 31.48) * mm, "end": v(-101.8, 8.26) * mm});
            skLineSegment(sketch, "E263.right", {"start": v(-113.99, 31.48) * mm, "end": v(-113.99, 8.26) * mm});
            skLineSegment(sketch, "E264.bottom", {"start": v(-125.03, 31.48) * mm, "end": v(-139.5, 31.48) * mm});
            skLineSegment(sketch, "E264.top", {"start": v(-125.03, 8.26) * mm, "end": v(-139.5, 8.26) * mm});
            skLineSegment(sketch, "E264.left", {"start": v(-125.03, 31.48) * mm, "end": v(-125.03, 8.26) * mm});
            skLineSegment(sketch, "E264.right", {"start": v(-139.5, 31.48) * mm, "end": v(-139.5, 8.26) * mm});
            skLineSegment(sketch, "E265.bottom", {"start": v(-82.4, -11.53) * mm, "end": v(-88.48, -11.53) * mm});
            skLineSegment(sketch, "E265.top", {"start": v(-82.4, -37.41) * mm, "end": v(-88.48, -37.41) * mm});
            skLineSegment(sketch, "E265.left", {"start": v(-82.4, -11.53) * mm, "end": v(-82.4, -37.41) * mm});
            skLineSegment(sketch, "E265.right", {"start": v(-88.48, -11.53) * mm, "end": v(-88.48, -37.41) * mm});
            skLineSegment(sketch, "E266.bottom", {"start": v(-98, -11.15) * mm, "end": v(-106, -11.15) * mm});
            skLineSegment(sketch, "E266.top", {"start": v(-98, -37.03) * mm, "end": v(-106, -37.03) * mm});
            skLineSegment(sketch, "E266.left", {"start": v(-98, -11.15) * mm, "end": v(-98, -37.03) * mm});
            skLineSegment(sketch, "E266.right", {"start": v(-106, -11.15) * mm, "end": v(-106, -37.03) * mm});
            skLineSegment(sketch, "E267.bottom", {"start": v(-113.23, -10.39) * mm, "end": v(-122.36, -10.39) * mm});
            skLineSegment(sketch, "E267.top", {"start": v(-113.23, -37.8) * mm, "end": v(-122.36, -37.8) * mm});
            skLineSegment(sketch, "E267.left", {"start": v(-113.23, -10.39) * mm, "end": v(-113.23, -37.8) * mm});
            skLineSegment(sketch, "E267.right", {"start": v(-122.36, -10.39) * mm, "end": v(-122.36, -37.8) * mm});
            skLineSegment(sketch, "E268.bottom", {"start": v(-129.21, -11.15) * mm, "end": v(-137.97, -11.15) * mm});
            skLineSegment(sketch, "E268.top", {"start": v(-129.21, -37.8) * mm, "end": v(-137.97, -37.8) * mm});
            skLineSegment(sketch, "E268.left", {"start": v(-129.21, -11.15) * mm, "end": v(-129.21, -37.8) * mm});
            skLineSegment(sketch, "E268.right", {"start": v(-137.97, -11.15) * mm, "end": v(-137.97, -37.8) * mm});
            skLineSegment(sketch, "E269.bottom", {"start": v(48.17, 37.2) * mm, "end": v(44.36, 37.2) * mm});
            skLineSegment(sketch, "E269.top", {"start": v(48.17, 10.55) * mm, "end": v(44.36, 10.55) * mm});
            skLineSegment(sketch, "E269.left", {"start": v(48.17, 37.2) * mm, "end": v(48.17, 10.55) * mm});
            skLineSegment(sketch, "E269.right", {"start": v(44.36, 37.2) * mm, "end": v(44.36, 10.55) * mm});
            skLineSegment(sketch, "E270.bottom", {"start": v(27.23, 37.2) * mm, "end": v(24.95, 37.2) * mm});
            skLineSegment(sketch, "E270.top", {"start": v(27.23, 10.55) * mm, "end": v(24.95, 10.55) * mm});
            skLineSegment(sketch, "E270.left", {"start": v(27.23, 37.2) * mm, "end": v(27.23, 10.55) * mm});
            skLineSegment(sketch, "E270.right", {"start": v(24.95, 37.2) * mm, "end": v(24.95, 10.55) * mm});
            skLineSegment(sketch, "E271.bottom", {"start": v(8.2, 37.2) * mm, "end": v(3.63, 37.2) * mm});
            skLineSegment(sketch, "E271.top", {"start": v(8.2, 10.55) * mm, "end": v(3.63, 10.55) * mm});
            skLineSegment(sketch, "E271.left", {"start": v(8.2, 37.2) * mm, "end": v(8.2, 10.55) * mm});
            skLineSegment(sketch, "E271.right", {"start": v(3.63, 37.2) * mm, "end": v(3.63, 10.55) * mm});
            skLineSegment(sketch, "E272.bottom", {"start": v(-11.21, 37.2) * mm, "end": v(-14.26, 37.2) * mm});
            skLineSegment(sketch, "E272.top", {"start": v(-11.21, 10.55) * mm, "end": v(-14.26, 10.55) * mm});
            skLineSegment(sketch, "E272.left", {"start": v(-11.21, 37.2) * mm, "end": v(-11.21, 10.55) * mm});
            skLineSegment(sketch, "E272.right", {"start": v(-14.26, 37.2) * mm, "end": v(-14.26, 10.55) * mm});
            skLineSegment(sketch, "E273.bottom", {"start": v(-35.2, 37.2) * mm, "end": v(-37.1, 37.2) * mm});
            skLineSegment(sketch, "E273.top", {"start": v(-35.2, 10.55) * mm, "end": v(-37.1, 10.55) * mm});
            skLineSegment(sketch, "E273.left", {"start": v(-35.2, 37.2) * mm, "end": v(-35.2, 10.55) * mm});
            skLineSegment(sketch, "E273.right", {"start": v(-37.1, 37.2) * mm, "end": v(-37.1, 10.55) * mm});
            skLineSegment(sketch, "E274.bottom", {"start": v(-53.46, 37.2) * mm, "end": v(-57.27, 37.2) * mm});
            skLineSegment(sketch, "E274.top", {"start": v(-53.46, 10.55) * mm, "end": v(-57.27, 10.55) * mm});
            skLineSegment(sketch, "E274.left", {"start": v(-53.46, 37.2) * mm, "end": v(-53.46, 10.55) * mm});
            skLineSegment(sketch, "E274.right", {"start": v(-57.27, 37.2) * mm, "end": v(-57.27, 10.55) * mm});
            skLineSegment(sketch, "E275", {"start": v(-142.92, 37.2) * mm, "end": v(-75.54, 37.2) * mm});
            skLineSegment(sketch, "E276", {"start": v(-142.92, 0) * mm, "end": v(138, 0) * mm});
            skSolve(sketch);
        }
        {
            var Q0;
            Q0=makeQuery(id+"F0.imprint","IMPRINT",FACE,{"disambiguationData":[TD([[makeQuery(id+"F0.imprint","IMPRINT",EDGE,{"derivedFrom":sQuery(id+"F0.wireOp",EDGE,"E0")}),-1.0]])]});
            extrude(context, id + "F4", {"entities" : qUnion([Q0]), "depth" : 5.08 * mm});
        }
        {
            var Q0;
            {var subQ0=sQuery(id+"F3.wireOp",EDGE,"E203");Q0=makeQuery(id+"F3.imprint","IMPRINT",FACE,{"disambiguationData":[TD([[makeQuery(id+"F3.imprint","IMPRINT",EDGE,{"derivedFrom":subQ0}),-1.0]])]});}
            var Q1;
            Q1=makeQuery(id+"F3.imprint","IMPRINT",FACE,{"disambiguationData":[TD([[makeQuery(id+"F3.imprint","IMPRINT",EDGE,{"derivedFrom":sQuery(id+"F3.wireOp",EDGE,"E262.bottom")}),-1.0]])]});
            var Q2;
            {var subQ5=sQuery(id+"F3.wireOp",EDGE,"E256");Q2=makeQuery(id+"F3.imprint","IMPRINT",FACE,{"disambiguationData":[TD([[makeQuery(id+"F3.imprint","IMPRINT",EDGE,{"derivedFrom":subQ5}),-1.0]])]});}
            var Q3;
            {var subQ0=sQuery(id+"F3.wireOp",EDGE,"E199");Q3=makeQuery(id+"F3.imprint","IMPRINT",FACE,{"disambiguationData":[TD([[makeQuery(id+"F3.imprint","IMPRINT",EDGE,{"derivedFrom":subQ0}),-1.0]])]});}
            var Q4;
            Q4=makeQuery(id+"F3.imprint","IMPRINT",FACE,{"disambiguationData":[TD([[makeQuery(id+"F3.imprint","IMPRINT",EDGE,{"derivedFrom":sQuery(id+"F3.wireOp",EDGE,"E258.bottom")}),-1.0]])]});
            var Q5;
            {var subQ0=sQuery(id+"F3.wireOp",EDGE,"E255");Q5=makeQuery(id+"F3.imprint","IMPRINT",FACE,{"disambiguationData":[TD([[makeQuery(id+"F3.imprint","IMPRINT",EDGE,{"derivedFrom":subQ0}),-1.0]])]});}
            var Q6;
            {var subQ0=sQuery(id+"F3.wireOp",EDGE,"E253");Q6=makeQuery(id+"F3.imprint","IMPRINT",FACE,{"disambiguationData":[TD([[makeQuery(id+"F3.imprint","IMPRINT",EDGE,{"derivedFrom":subQ0}),-1.0]])]});}
            var Q7;
            {var subQ0=sQuery(id+"F3.wireOp",EDGE,"E251");Q7=makeQuery(id+"F3.imprint","IMPRINT",FACE,{"disambiguationData":[TD([[makeQuery(id+"F3.imprint","IMPRINT",EDGE,{"derivedFrom":subQ0}),-1.0]])]});}
            var Q8;
            {var subQ0=sQuery(id+"F3.wireOp",EDGE,"E244");Q8=makeQuery(id+"F3.imprint","IMPRINT",FACE,{"disambiguationData":[TD([[makeQuery(id+"F3.imprint","IMPRINT",EDGE,{"derivedFrom":subQ0}),1.0]])]});}
            var Q9;
            {var subQ0=sQuery(id+"F3.wireOp",EDGE,"E240");Q9=makeQuery(id+"F3.imprint","IMPRINT",FACE,{"disambiguationData":[TD([[makeQuery(id+"F3.imprint","IMPRINT",EDGE,{"derivedFrom":subQ0}),1.0]])]});}
            var Q10;
            {var subQ4=sQuery(id+"F3.wireOp",EDGE,"E237");Q10=makeQuery(id+"F3.imprint","IMPRINT",FACE,{"disambiguationData":[TD([[makeQuery(id+"F3.imprint","IMPRINT",EDGE,{"derivedFrom":subQ4}),1.0]])]});}
            var Q11;
            {var subQ0=sQuery(id+"F3.wireOp",EDGE,"E248");Q11=makeQuery(id+"F3.imprint","IMPRINT",FACE,{"disambiguationData":[TD([[makeQuery(id+"F3.imprint","IMPRINT",EDGE,{"derivedFrom":subQ0}),1.0]])]});}
            var Q12;
            {var subQ1=sQuery(id+"F3.wireOp",EDGE,"E219");Q12=makeQuery(id+"F3.imprint","IMPRINT",FACE,{"disambiguationData":[TD([[makeQuery(id+"F3.imprint","IMPRINT",EDGE,{"derivedFrom":subQ1}),1.0]])]});}
            extrude(context, id + "F5", {"entities" : qUnion([Q0, Q1, Q2, Q3, Q4, Q5, Q6, Q7, Q8, Q9, Q10, Q11, Q12]), "operationType" : NewBodyOperationType.ADD, "depth" : 5.08 * mm});
        }
        {
            var Q0;
            {var subQ10=sQuery(id+"F1.wireOp",EDGE,"E105");Q0=makeQuery(id+"F1.imprint","IMPRINT",FACE,{"disambiguationData":[TD([[makeQuery(id+"F1.imprint","IMPRINT",EDGE,{"derivedFrom":subQ10}),-1.0]])]});}
            var Q1;
            Q1=makeQuery(id+"F2.imprint","IMPRINT",FACE,{"disambiguationData":[TD([[makeQuery(id+"F2.imprint","IMPRINT",EDGE,{"derivedFrom":sQuery(id+"F2.wireOp",EDGE,"E171")}),1.0]])]});
            var Q2;
            {var subQ0=sQuery(id+"F2.wireOp",EDGE,"E188");Q2=makeQuery(id+"F2.imprint","IMPRINT",FACE,{"disambiguationData":[TD([[makeQuery(id+"F2.imprint","IMPRINT",EDGE,{"derivedFrom":subQ0}),1.0]])]});}
            var Q3;
            {var subQ0=sQuery(id+"F1.wireOp",EDGE,"E113");var subQ1=sQuery(id+"F1.wireOp",EDGE,"E108");var subQ2=makeQuery(id+"F1.imprint","INTERSECT",VERTEX,{"derivedFrom":[subQ1,subQ0]});Q3=makeQuery(id+"F1.imprint","IMPRINT",FACE,{"disambiguationData":[TD([[makeQuery(id+"F1.imprint","IMPRINT",EDGE,{"disambiguationData":[TD([[subQ2,-1.0]])],"derivedFrom":subQ1}),-1.0]])]});}
            var Q4;
            Q4=makeQuery(id+"F2.imprint","IMPRINT",FACE,{"disambiguationData":[TD([[makeQuery(id+"F2.imprint","IMPRINT",EDGE,{"derivedFrom":sQuery(id+"F2.wireOp",EDGE,"E179")}),1.0]])]});
            var Q5;
            {var subQ10=sQuery(id+"F2.wireOp",EDGE,"E150");Q5=makeQuery(id+"F2.imprint","IMPRINT",FACE,{"disambiguationData":[TD([[makeQuery(id+"F2.imprint","IMPRINT",EDGE,{"derivedFrom":subQ10}),-1.0]])]});}
            var Q6;
            {var subQ0=sQuery(id+"F1.wireOp",EDGE,"E115");Q6=makeQuery(id+"F1.imprint","IMPRINT",FACE,{"disambiguationData":[TD([[makeQuery(id+"F1.imprint","IMPRINT",EDGE,{"derivedFrom":subQ0}),1.0]])]});}
            var Q7;
            {var subQ3=sQuery(id+"F2.wireOp",EDGE,"E150");Q7=makeQuery(id+"F2.imprint","IMPRINT",FACE,{"disambiguationData":[TD([[makeQuery(id+"F2.imprint","IMPRINT",EDGE,{"derivedFrom":subQ3}),1.0]])]});}
            extrude(context, id + "F6", {"entities" : qUnion([Q0, Q1, Q2, Q3, Q4, Q5, Q6, Q7]), "depth" : 5.08 * mm});
        }
    });
